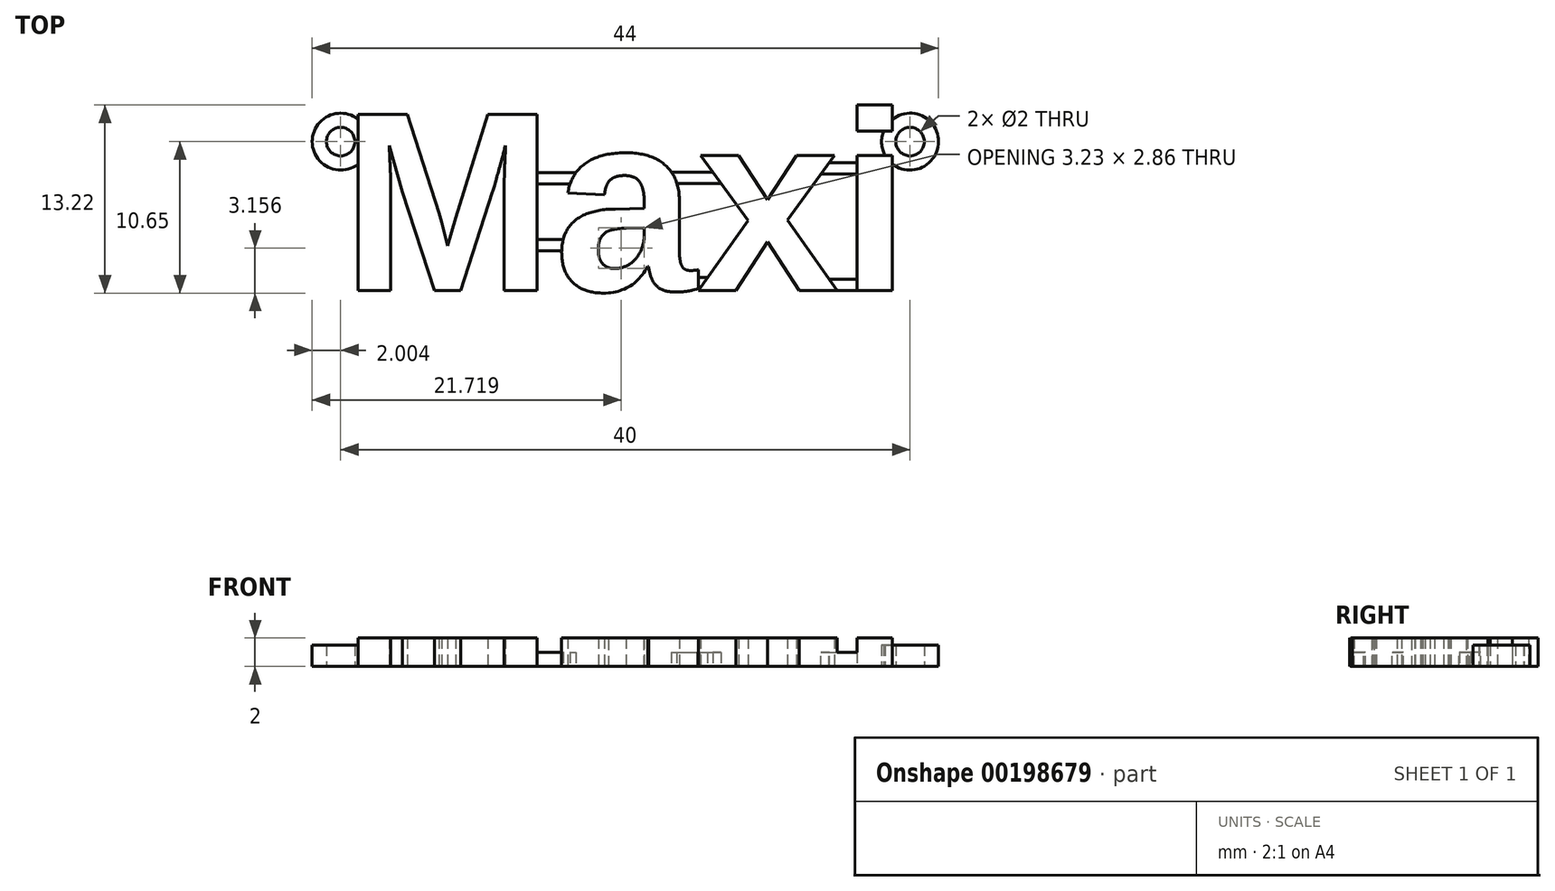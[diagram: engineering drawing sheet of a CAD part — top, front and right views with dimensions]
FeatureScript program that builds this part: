
annotation { "Feature Type Name" : "Feature", "Feature Type Description" : "" }
export const myFeature = defineFeature(function(context is Context, id is Id, definition is map)
    precondition{}
    {
        {
            var Q0;
            Q0=qCreatedBy(makeId("Top.planeOp"),FACE);
            var sketch = newSketch(context, id + "F0", { "sketchPlane" : qUnion([Q0])});
            skText(sketch, "E0", { "text": "Maxi", "fontName": "Arimo-Bold.ttf"});
            const initialGuessF0  = {"E0": [-0.0161, -0.00579, 1, 0, 0.01296]};
            skSetInitialGuess(sketch, initialGuessF0);
            skSolve(sketch);
        }
        {
            var Q0;
            Q0=makeQuery(id+"F0.imprint","IMPRINT",FACE,{"disambiguationData":[TD([[makeQuery(id+"F0.imprint","IMPRINT",EDGE,{"derivedFrom":sQuery(id+"F0.wireOp",EDGE,"E0.sketch_text.stroke-0")}),-1.0]])]});
            var sketch = newSketch(context, id + "F1", { "sketchPlane" : qUnion([Q0])});
            skCircle(sketch, "E1", {"center": v(-16.1, 4.68) * mm, "radius": 2 * mm});
            skCircle(sketch, "E2", {"center": v(-16.1, 4.68) * mm, "radius": 1 * mm});
            skCircle(sketch, "E3", {"center": v(23.9, 4.68) * mm, "radius": 2 * mm});
            skCircle(sketch, "E4", {"center": v(23.9, 4.68) * mm, "radius": 1 * mm});
            skLineSegment(sketch, "E5.bottom", {"start": v(-3, -2.2) * mm, "end": v(0, -2.2) * mm});
            skLineSegment(sketch, "E5.top", {"start": v(-3, -3) * mm, "end": v(0, -3) * mm});
            skLineSegment(sketch, "E5.left", {"start": v(-3, -2.2) * mm, "end": v(-3, -3) * mm});
            skLineSegment(sketch, "E5.right", {"start": v(0, -2.2) * mm, "end": v(0, -3) * mm});
            skLineSegment(sketch, "E6.bottom", {"start": v(-4.36, 2.5) * mm, "end": v(0.64, 2.5) * mm});
            skLineSegment(sketch, "E6.top", {"start": v(-4.36, 1.7) * mm, "end": v(0.64, 1.7) * mm});
            skLineSegment(sketch, "E6.left", {"start": v(-4.36, 2.5) * mm, "end": v(-4.36, 1.7) * mm});
            skLineSegment(sketch, "E6.right", {"start": v(0.64, 2.5) * mm, "end": v(0.64, 1.7) * mm});
            skLineSegment(sketch, "E7.bottom", {"start": v(6.85, 2.53) * mm, "end": v(10.85, 2.53) * mm});
            skLineSegment(sketch, "E7.top", {"start": v(6.85, 1.73) * mm, "end": v(10.85, 1.73) * mm});
            skLineSegment(sketch, "E7.left", {"start": v(6.85, 2.53) * mm, "end": v(6.85, 1.73) * mm});
            skLineSegment(sketch, "E7.right", {"start": v(10.85, 2.53) * mm, "end": v(10.85, 1.73) * mm});
            skLineSegment(sketch, "E8.bottom", {"start": v(16.77, 3.21) * mm, "end": v(20.77, 3.21) * mm});
            skLineSegment(sketch, "E8.top", {"start": v(16.77, 2.41) * mm, "end": v(20.77, 2.41) * mm});
            skLineSegment(sketch, "E8.left", {"start": v(16.77, 3.21) * mm, "end": v(16.77, 2.41) * mm});
            skLineSegment(sketch, "E8.right", {"start": v(20.77, 3.21) * mm, "end": v(20.77, 2.41) * mm});
            skLineSegment(sketch, "E9.bottom", {"start": v(16.77, -4.99) * mm, "end": v(20.77, -4.99) * mm});
            skLineSegment(sketch, "E9.top", {"start": v(16.77, -5.79) * mm, "end": v(20.77, -5.79) * mm});
            skLineSegment(sketch, "E9.left", {"start": v(16.77, -4.99) * mm, "end": v(16.77, -5.79) * mm});
            skLineSegment(sketch, "E9.right", {"start": v(20.77, -4.99) * mm, "end": v(20.77, -5.79) * mm});
            skLineSegment(sketch, "E10.bottom", {"start": v(7.01, -4.87) * mm, "end": v(11.01, -4.87) * mm});
            skLineSegment(sketch, "E10.top", {"start": v(7.01, -5.67) * mm, "end": v(11.01, -5.67) * mm});
            skLineSegment(sketch, "E10.left", {"start": v(7.01, -4.87) * mm, "end": v(7.01, -5.67) * mm});
            skLineSegment(sketch, "E10.right", {"start": v(11.01, -4.87) * mm, "end": v(11.01, -5.67) * mm});
            skSolve(sketch);
        }
        {
            var Q0;
            Q0 = qSketchRegion(id + "F0", true);
            extrude(context, id + "F2", {"entities" : qUnion([Q0]), "depth" : 2 * mm});
        }
        {
            var Q0;
            Q0 = qSketchRegion(id + "F1", true);
            extrude(context, id + "F3", {"entities" : qUnion([Q0]), "operationType" : NewBodyOperationType.ADD, "depth" : 1 * mm});
        }
        {
            var Q0;
            Q0=makeQuery(id+"F1.imprint","IMPRINT",FACE,{"disambiguationData":[TD([[makeQuery(id+"F1.imprint","IMPRINT",EDGE,{"derivedFrom":sQuery(id+"F1.wireOp",EDGE,"E2")}),-1.0]])]});
            var Q1;
            Q1=makeQuery(id+"F1.imprint","IMPRINT",FACE,{"disambiguationData":[TD([[makeQuery(id+"F1.imprint","IMPRINT",EDGE,{"derivedFrom":sQuery(id+"F1.wireOp",EDGE,"E3")}),1.0]])]});
            extrude(context, id + "F4", {"entities" : qUnion([Q0, Q1]), "operationType" : NewBodyOperationType.ADD, "depth" : 1.5 * mm});
        }
    });
